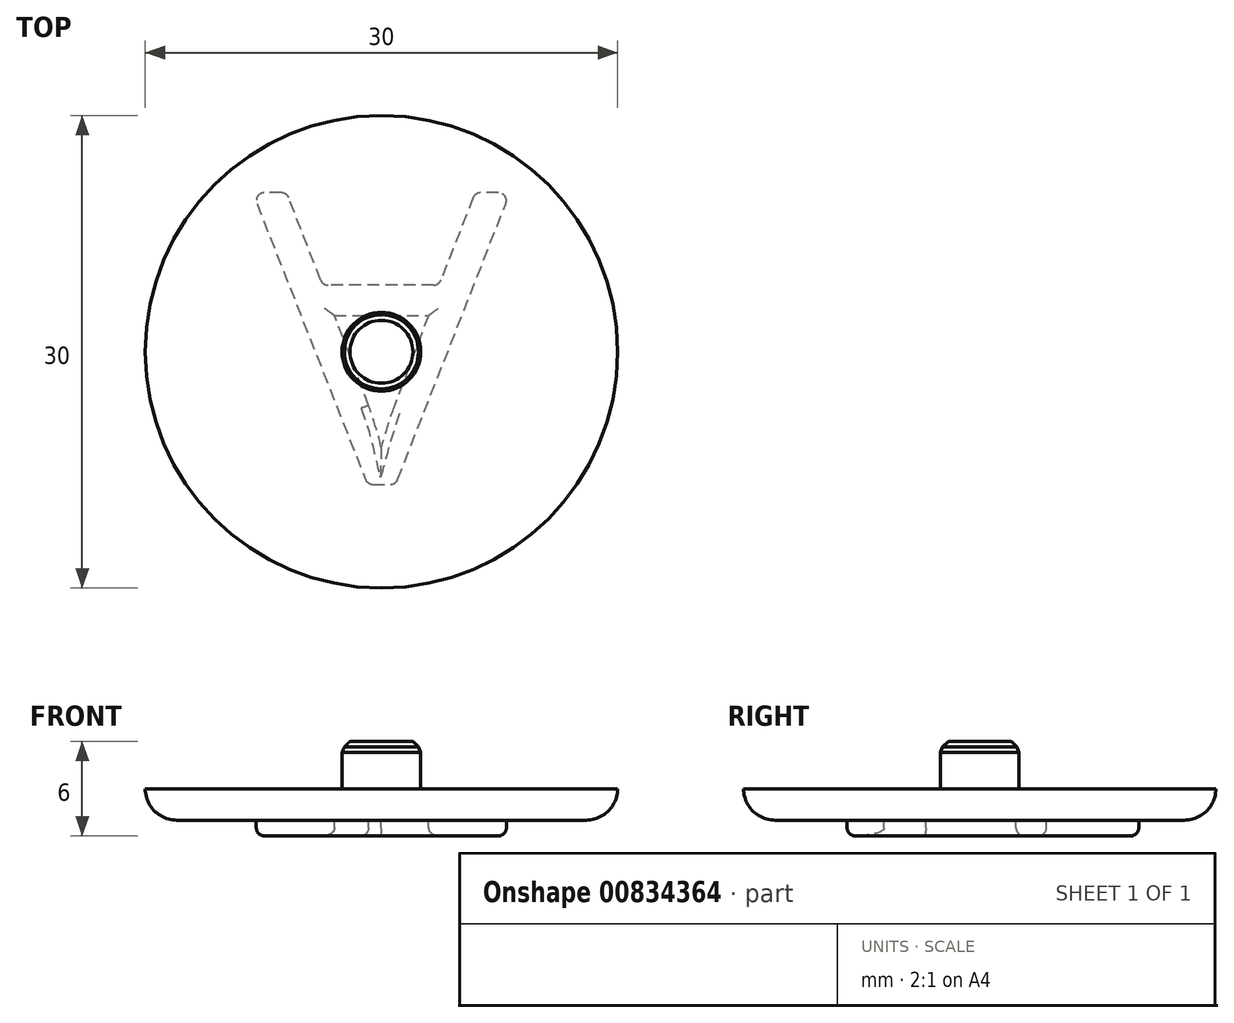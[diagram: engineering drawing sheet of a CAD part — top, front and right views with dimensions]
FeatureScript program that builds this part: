
annotation { "Feature Type Name" : "Feature", "Feature Type Description" : "" }
export const myFeature = defineFeature(function(context is Context, id is Id, definition is map)
    precondition{}
    {
        {
            var Q0;
            Q0=qCreatedBy(makeId("Top.planeOp"),FACE);
            var sketch = newSketch(context, id + "F0", { "sketchPlane" : qUnion([Q0])});
            skCircle(sketch, "E0", {"center": v(0, 0) * mm, "radius": 15 * mm});
            skSolve(sketch);
        }
        {
            var Q0;
            Q0 = qSketchRegion(id + "F0", true);
            extrude(context, id + "F1", {"entities" : qUnion([Q0]), "depth" : 2 * mm, "offsetDistance" : 25 * mm});
        }
        {
            var Q0;
            Q0=makeQuery(id+"F1.opExtrude","CAP_FACE",FACE,{"disambiguationData":[OSD([sQuery(id+"F0.wireOp",EDGE,"E0")])],"isStart":false});
            var sketch = newSketch(context, id + "F2", { "sketchPlane" : qUnion([Q0])});
            skCircle(sketch, "E1", {"center": v(0, 0) * mm, "radius": 2.5 * mm});
            skSolve(sketch);
        }
        {
            var Q0;
            Q0 = qSketchRegion(id + "F2", true);
            extrude(context, id + "F3", {"entities" : qUnion([Q0]), "operationType" : NewBodyOperationType.ADD, "depth" : 3 * mm, "offsetDistance" : 25 * mm});
        }
        {
            var Q0;
            Q0=makeQuery(id+"F1.opExtrude","CAP_EDGE",EDGE,{"disambiguationData":[OSD([sQuery(id+"F0.wireOp",EDGE,"E0")])],"isStart":true});
            fillet(context, id + "F4", {"entities" : qUnion([Q0]), "radius" : 2 * mm, "tangentPropagation" : true, "allowEdgeOverflow" : false});
        }
        {
            var Q0;
            Q0=makeQuery(id+"F3.opExtrude","CAP_EDGE",EDGE,{"disambiguationData":[OSD([sQuery(id+"F2.wireOp",EDGE,"E1")])],"isStart":false});
            chamfer(context, id + "F5", {"entities" : qUnion([Q0]), "width" : 0.5 * mm, "tangentPropagation" : true});
        }
        {
            var Q0;
            {var subQ0=sQuery(id+"F2.wireOp",EDGE,"E1");Q0=makeQuery(id+"F5.opChamfer","BLEND_EDGE",EDGE,{"blendedFrom":[makeQuery(id+"F3.opExtrude","CAP_EDGE",EDGE,{"disambiguationData":[OSD([subQ0])],"isStart":false}),makeQuery(id+"F3.opExtrude","SWEPT_FACE",FACE,{"disambiguationData":[OSD([subQ0])]})],"blendedInto":[makeQuery(id+"F3.opExtrude","SWEPT_FACE",FACE,{"disambiguationData":[OSD([subQ0])]})]});}
            chamfer(context, id + "F6", {"entities" : qUnion([Q0]), "width" : 0.5 * mm, "tangentPropagation" : true});
        }
        {
            var Q0;
            Q0=makeQuery(id+"F1.opExtrude","CAP_FACE",FACE,{"disambiguationData":[OSD([sQuery(id+"F0.wireOp",EDGE,"E0")])],"isStart":true});
            var sketch = newSketch(context, id + "F7", { "sketchPlane" : qUnion([Q0])});
            skText(sketch, "E2", { "text": "A", "fontName": "OpenSans-Regular.ttf"});
            const initialGuessF7  = {"E2": [-0.00818, -0.0101, 1, 0, 0.0186]};
            skSetInitialGuess(sketch, initialGuessF7);
            skSolve(sketch);
        }
        {
            var Q0;
            Q0=makeQuery(id+"F7.imprint","IMPRINT",FACE,{"disambiguationData":[TD([[makeQuery(id+"F7.imprint","IMPRINT",EDGE,{"derivedFrom":sQuery(id+"F7.wireOp",EDGE,"E2.sketch_text.stroke-0")}),-1.0]])]});
            extrude(context, id + "F8", {"entities" : qUnion([Q0]), "operationType" : NewBodyOperationType.ADD, "depth" : 1 * mm, "offsetDistance" : 25 * mm});
        }
        {
            var Q0;
            Q0=makeQuery(id+"F8.opExtrude","CAP_EDGE",EDGE,{"disambiguationData":[OSD([sQuery(id+"F7.wireOp",EDGE,"E2.sketch_text.stroke-4")])],"isStart":false});
            var Q1;
            Q1=makeQuery(id+"F8.opExtrude","CAP_EDGE",EDGE,{"disambiguationData":[OSD([sQuery(id+"F7.wireOp",EDGE,"E2.sketch_text.stroke-3")])],"isStart":false});
            var Q2;
            Q2=makeQuery(id+"F8.opExtrude","CAP_EDGE",EDGE,{"disambiguationData":[OSD([sQuery(id+"F7.wireOp",EDGE,"E2.sketch_text.stroke-2")])],"isStart":false});
            var Q3;
            Q3=makeQuery(id+"F8.opExtrude","CAP_EDGE",EDGE,{"disambiguationData":[OSD([sQuery(id+"F7.wireOp",EDGE,"E2.sketch_text.stroke-1")])],"isStart":false});
            var Q4;
            Q4=makeQuery(id+"F8.opExtrude","CAP_FACE",FACE,{"disambiguationData":[OSD([sQuery(id+"F7.wireOp",EDGE,"E2.sketch_text.stroke-0"),sQuery(id+"F7.wireOp",EDGE,"E2.sketch_text.stroke-1"),sQuery(id+"F7.wireOp",EDGE,"E2.sketch_text.stroke-2"),sQuery(id+"F7.wireOp",EDGE,"E2.sketch_text.stroke-3"),sQuery(id+"F7.wireOp",EDGE,"E2.sketch_text.stroke-4"),sQuery(id+"F7.wireOp",EDGE,"E2.sketch_text.stroke-5"),sQuery(id+"F7.wireOp",EDGE,"E2.sketch_text.stroke-6"),sQuery(id+"F7.wireOp",EDGE,"E2.sketch_text.stroke-7"),sQuery(id+"F7.wireOp",EDGE,"E2.sketch_text.stroke-8"),sQuery(id+"F7.wireOp",EDGE,"E2.sketch_text.stroke-9"),sQuery(id+"F7.wireOp",EDGE,"E2.sketch_text.stroke-10"),sQuery(id+"F7.wireOp",EDGE,"E2.sketch_text.stroke-11"),sQuery(id+"F7.wireOp",EDGE,"E2.sketch_text.stroke-12")])],"isStart":false});
            var Q5;
            Q5=makeQuery(id+"F8.opExtrude","SWEPT_EDGE",EDGE,{"disambiguationData":[OSD([sQuery(id+"F7.wireOp",EDGE,"E2.sketch_text.stroke-0"),sQuery(id+"F7.wireOp",EDGE,"E2.sketch_text.stroke-7")])]});
            var Q6;
            Q6=makeQuery(id+"F8.opExtrude","SWEPT_EDGE",EDGE,{"disambiguationData":[OSD([sQuery(id+"F7.wireOp",EDGE,"E2.sketch_text.stroke-6"),sQuery(id+"F7.wireOp",EDGE,"E2.sketch_text.stroke-7")])]});
            var Q7;
            Q7=makeQuery(id+"F8.opExtrude","SWEPT_EDGE",EDGE,{"disambiguationData":[OSD([sQuery(id+"F7.wireOp",EDGE,"E2.sketch_text.stroke-0"),sQuery(id+"F7.wireOp",EDGE,"E2.sketch_text.stroke-1")])]});
            var Q8;
            Q8=makeQuery(id+"F8.opExtrude","SWEPT_EDGE",EDGE,{"disambiguationData":[OSD([sQuery(id+"F7.wireOp",EDGE,"E2.sketch_text.stroke-1"),sQuery(id+"F7.wireOp",EDGE,"E2.sketch_text.stroke-2")])]});
            var Q9;
            Q9=makeQuery(id+"F8.opExtrude","SWEPT_EDGE",EDGE,{"disambiguationData":[OSD([sQuery(id+"F7.wireOp",EDGE,"E2.sketch_text.stroke-2"),sQuery(id+"F7.wireOp",EDGE,"E2.sketch_text.stroke-3")])]});
            var Q10;
            Q10=makeQuery(id+"F8.opExtrude","SWEPT_EDGE",EDGE,{"disambiguationData":[OSD([sQuery(id+"F0.wireOp",EDGE,"E0"),sQuery(id+"F7.wireOp",EDGE,"E2.sketch_text.stroke-3"),sQuery(id+"F7.wireOp",EDGE,"E2.sketch_text.stroke-4")])]});
            var Q11;
            Q11=makeQuery(id+"F8.opExtrude","SWEPT_EDGE",EDGE,{"disambiguationData":[OSD([sQuery(id+"F7.wireOp",EDGE,"E2.sketch_text.stroke-5"),sQuery(id+"F7.wireOp",EDGE,"E2.sketch_text.stroke-6")])]});
            var Q12;
            Q12=makeQuery(id+"F8.opExtrude","SWEPT_EDGE",EDGE,{"disambiguationData":[OSD([sQuery(id+"F7.wireOp",EDGE,"E2.sketch_text.stroke-4"),sQuery(id+"F7.wireOp",EDGE,"E2.sketch_text.stroke-5")])]});
            fillet(context, id + "F9", {"entities" : qUnion([Q0, Q1, Q2, Q3, Q4, Q5, Q6, Q7, Q8, Q9, Q10, Q11, Q12]), "radius" : 0.5 * mm, "tangentPropagation" : true, "allowEdgeOverflow" : false});
        }
    });
